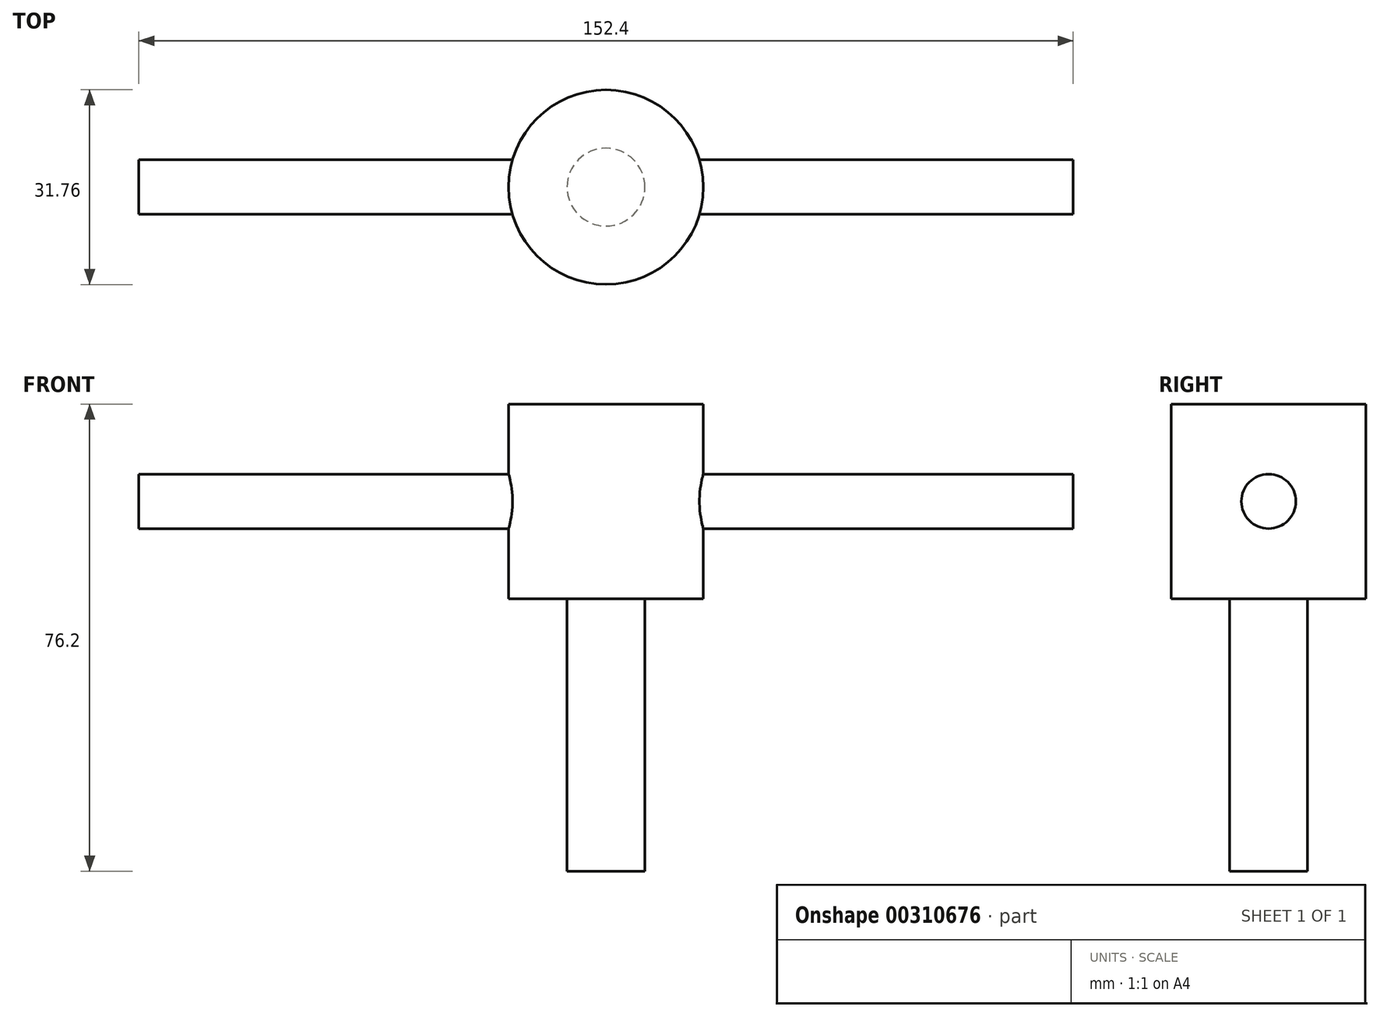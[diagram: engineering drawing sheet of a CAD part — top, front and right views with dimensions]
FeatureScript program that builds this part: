
annotation { "Feature Type Name" : "Feature", "Feature Type Description" : "" }
export const myFeature = defineFeature(function(context is Context, id is Id, definition is map)
    precondition{}
    {
        {
            var Q0;
            Q0=qCreatedBy(makeId("Top.planeOp"),FACE);
            var sketch = newSketch(context, id + "F0", { "sketchPlane" : qUnion([Q0])});
            skCircle(sketch, "E0", {"center": v(0, 0) * mm, "radius": 15.88 * mm});
            skSolve(sketch);
        }
        {
            var Q0;
            Q0 = qSketchRegion(id + "F0", true);
            extrude(context, id + "F1", {"entities" : qUnion([Q0]), "depth" : 76.2 * mm});
        }
        {
            var Q0;
            Q0=makeQuery(id+"F1.opExtrude","CAP_FACE",FACE,{"disambiguationData":[OSD([sQuery(id+"F0.wireOp",EDGE,"E0")])],"isStart":true});
            var sketch = newSketch(context, id + "F2", { "sketchPlane" : qUnion([Q0])});
            skCircle(sketch, "E1", {"center": v(0, 0) * mm, "radius": 6.35 * mm});
            skCircle(sketch, "E2", {"center": v(0, 0) * mm, "radius": 15.88 * mm});
            skSolve(sketch);
        }
        {
            var Q0;
            Q0 = qSketchRegion(id + "F2", true);
            extrude(context, id + "F3", {"entities" : qUnion([Q0]), "operationType" : NewBodyOperationType.REMOVE, "oppositeDirection" : true, "depth" : 44.45 * mm});
        }
        {
            var Q0;
            Q0=qCreatedBy(makeId("Right.planeOp"),FACE);
            var sketch = newSketch(context, id + "F4", { "sketchPlane" : qUnion([Q0])});
            skCircle(sketch, "E3", {"center": v(0, 60.33) * mm, "radius": 4.45 * mm});
            skSolve(sketch);
        }
        {
            var Q0;
            Q0 = qSketchRegion(id + "F4", true);
            extrude(context, id + "F5", {"entities" : qUnion([Q0]), "operationType" : NewBodyOperationType.ADD, "endBound" : BoundingType.SYMMETRIC, "depth" : 152.4 * mm});
        }
    });
